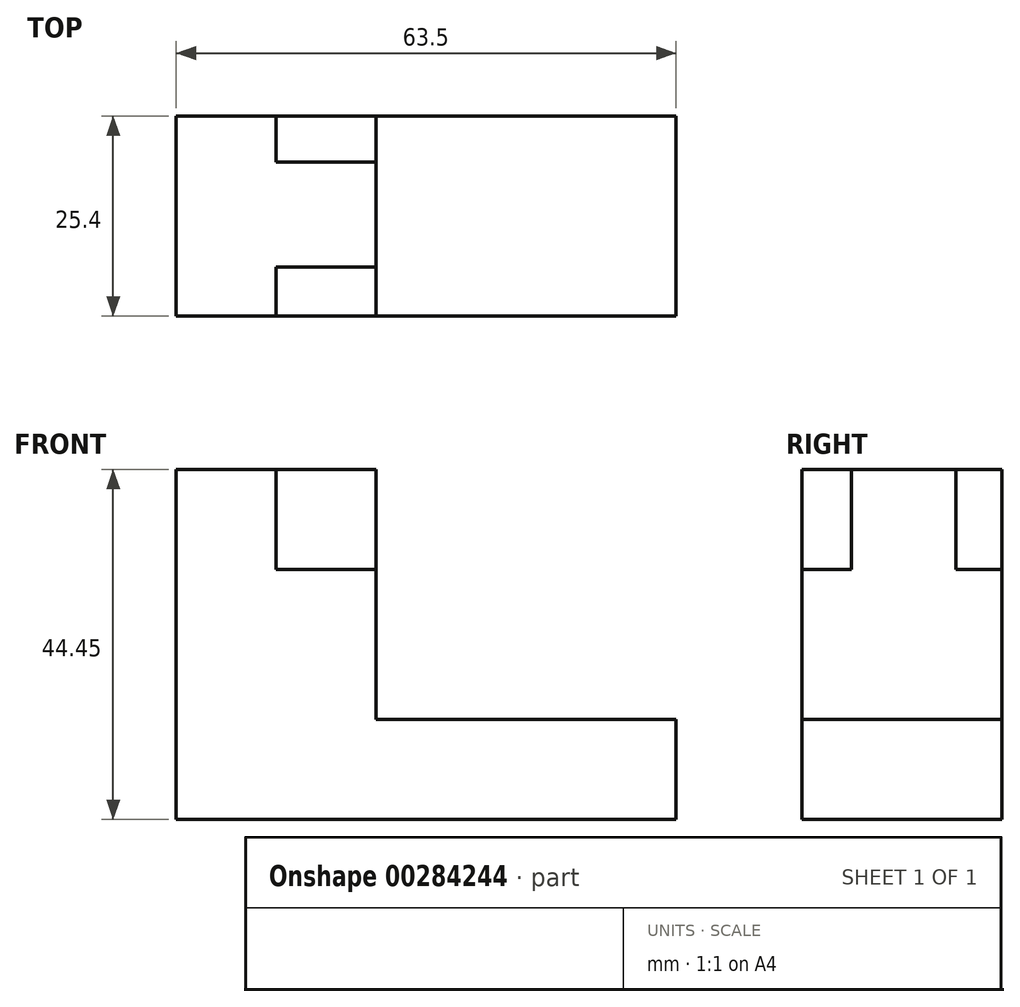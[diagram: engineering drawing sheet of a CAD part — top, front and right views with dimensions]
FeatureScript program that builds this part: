
annotation { "Feature Type Name" : "Feature", "Feature Type Description" : "" }
export const myFeature = defineFeature(function(context is Context, id is Id, definition is map)
    precondition{}
    {
        {
            var Q0;
            Q0=qCreatedBy(makeId("Front.planeOp"),FACE);
            var sketch = newSketch(context, id + "F0", { "sketchPlane" : qUnion([Q0])});
            skLineSegment(sketch, "E0", {"start": v(0, 0) * mm, "end": v(63.5, 0) * mm});
            skLineSegment(sketch, "E1", {"start": v(63.5, 0) * mm, "end": v(63.5, 12.7) * mm});
            skLineSegment(sketch, "E2", {"start": v(63.5, 12.7) * mm, "end": v(38.1, 12.7) * mm});
            skLineSegment(sketch, "E3", {"start": v(38.1, 12.7) * mm, "end": v(38.1, 19.05) * mm});
            skLineSegment(sketch, "E4", {"start": v(38.1, 19.05) * mm, "end": v(12.7, 19.05) * mm});
            skLineSegment(sketch, "E5", {"start": v(12.7, 19.05) * mm, "end": v(12.7, 44.45) * mm});
            skLineSegment(sketch, "E6", {"start": v(12.7, 44.45) * mm, "end": v(0, 44.45) * mm});
            skLineSegment(sketch, "E7", {"start": v(0, 44.45) * mm, "end": v(0, 31.75) * mm});
            skLineSegment(sketch, "E8", {"start": v(0, 31.75) * mm, "end": v(0, 0) * mm});
            skLineSegment(sketch, "E9", {"start": v(12.7, 44.45) * mm, "end": v(25.4, 44.45) * mm});
            skLineSegment(sketch, "E10", {"start": v(25.4, 44.45) * mm, "end": v(25.4, 31.75) * mm});
            skLineSegment(sketch, "E11", {"start": v(25.4, 31.75) * mm, "end": v(38.1, 31.75) * mm});
            skLineSegment(sketch, "E12", {"start": v(38.1, 31.75) * mm, "end": v(38.1, 19.05) * mm});
            skSolve(sketch);
        }
        {
            var Q0;
            Q0 = qSketchRegion(id + "F0", true);
            extrude(context, id + "F1", {"entities" : qUnion([Q0]), "depth" : 25.4 * mm});
        }
        {
            var Q0;
            Q0=makeQuery(id+"F1.opExtrude","SWEPT_FACE",FACE,{"disambiguationData":[OSD([sQuery(id+"F0.wireOp",EDGE,"E10")])]});
            var sketch = newSketch(context, id + "F2", { "sketchPlane" : qUnion([Q0])});
            skLineSegment(sketch, "E13", {"start": v(-19.15, 44.45) * mm, "end": v(-19.15, 24.29) * mm});
            skLineSegment(sketch, "E14", {"start": v(-19.15, 24.29) * mm, "end": v(-25.4, 24.29) * mm});
            skLineSegment(sketch, "E15", {"start": v(-5.84, 44.45) * mm, "end": v(-5.84, 24.08) * mm});
            skLineSegment(sketch, "E16", {"start": v(-5.84, 24.08) * mm, "end": v(0, 24.08) * mm});
            skSolve(sketch);
        }
        {
            var Q0;
            Q0 = qSketchRegion(id + "F2", true);
            var Q1;
            {var subQ1=sQuery(id+"F0.wireOp",EDGE,"E10");var subQ6=makeQuery(id+"F1.opExtrude","CAP_EDGE",EDGE,{"disambiguationData":[OSD([subQ1])],"isStart":false});Q1=makeQuery(id+"F2.imprint","IMPRINT",FACE,{"disambiguationData":[TD([[makeQuery(id+"F2.imprint","IMPRINT",EDGE,{"derivedFrom":subQ6}),1.0]])]});}
            var Q2;
            {var subQ1=sQuery(id+"F0.wireOp",EDGE,"E10");var subQ6=makeQuery(id+"F1.opExtrude","CAP_EDGE",EDGE,{"disambiguationData":[OSD([subQ1])],"isStart":true});Q2=makeQuery(id+"F2.imprint","IMPRINT",FACE,{"disambiguationData":[TD([[makeQuery(id+"F2.imprint","IMPRINT",EDGE,{"derivedFrom":subQ6}),-1.0]])]});}
            var Q3;
            Q3=makeQuery(id+"F1.opExtrude","SWEPT_FACE",FACE,{"disambiguationData":[OSD([sQuery(id+"F0.wireOp",EDGE,"E3"),sQuery(id+"F0.wireOp",EDGE,"E12")])]});
            extrude(context, id + "F3", {"entities" : qUnion([Q0, Q1, Q2, Q3]), "operationType" : NewBodyOperationType.REMOVE, "endBound" : BoundingType.SYMMETRIC, "oppositeDirection" : true, "depth" : 25.4 * mm});
        }
    });
